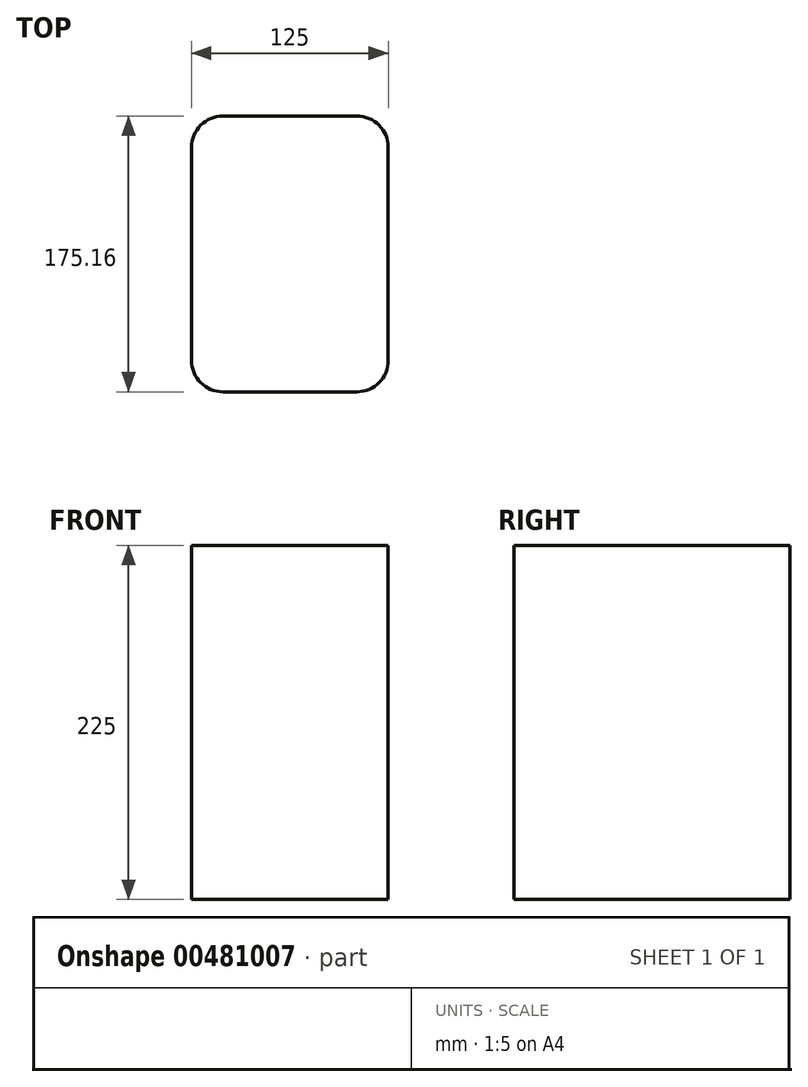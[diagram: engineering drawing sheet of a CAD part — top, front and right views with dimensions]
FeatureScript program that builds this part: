
annotation { "Feature Type Name" : "Feature", "Feature Type Description" : "" }
export const myFeature = defineFeature(function(context is Context, id is Id, definition is map)
    precondition{}
    {
        {
            var Q0;
            Q0=qCreatedBy(makeId("Top.planeOp"),FACE);
            var sketch = newSketch(context, id + "F0", { "sketchPlane" : qUnion([Q0])});
            skLineSegment(sketch, "E0", {"start": v(-48.18, 95.54) * mm, "end": v(36.82, 95.54) * mm});
            skLineSegment(sketch, "E1", {"start": v(56.82, 75.54) * mm, "end": v(56.82, -59.62) * mm});
            skLineSegment(sketch, "E2", {"start": v(36.82, -79.62) * mm, "end": v(-48.18, -79.62) * mm});
            skPoint(sketch, "E3.visualSharp", {"position": v(56.82, 95.54) * mm});
            skArc(sketch, "E3.filletArc", {"start": v(56.82, 75.54) * mm, "mid": v(50.96, 89.69) * mm, "end": v(36.82, 95.54) * mm});
            skPoint(sketch, "E4.visualSharp", {"position": v(56.82, -79.62) * mm});
            skArc(sketch, "E4.filletArc", {"start": v(36.82, -79.62) * mm, "mid": v(50.96, -73.76) * mm, "end": v(56.82, -59.62) * mm});
            skLineSegment(sketch, "E5", {"start": v(-68.18, -59.62) * mm, "end": v(-68.18, 75.54) * mm});
            skArc(sketch, "E6.filletArc", {"start": v(-48.18, 95.54) * mm, "mid": v(-62.32, 89.69) * mm, "end": v(-68.18, 75.54) * mm});
            skPoint(sketch, "E7.visualSharp", {"position": v(-68.18, -79.62) * mm});
            skArc(sketch, "E7.filletArc", {"start": v(-68.18, -59.62) * mm, "mid": v(-62.32, -73.76) * mm, "end": v(-48.18, -79.62) * mm});
            skSolve(sketch);
        }
        {
            var Q0;
            Q0=qSketchRegion(id+"F0",true);
            extrude(context, id + "F1", {"entities" : qUnion([Q0]), "depth" : 225 * mm});
        }
    });
